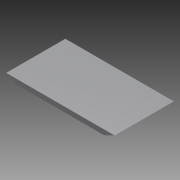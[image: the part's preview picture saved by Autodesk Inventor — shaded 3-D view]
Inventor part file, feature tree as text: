
AUTODESK INVENTOR PART (.ipt)
format: ipt  version: 2012 (Build 160160000, 160)  size: 70,656 bytes
history: native  units: in
note: dims shown in document units (in); Inventor stores cm internally (conversion verified against a paired STEP export)
features: extrude x1, sketch x1
ambient origin geometry x8: Origin, YZ Plane, XZ Plane, XY Plane, X Axis, Y Axis, Z Axis, Center Point
bodies: Solid1 (feature_tree)
feature tree (2):
  extrude  "Extrusion1"  Depth=9.5in
  sketch  "Sketch1"  dims[d1=88.0in d2=9.5in d3=9.5in d4=48.0in d5=0.0in d7=8.0in d8=2.0in]
